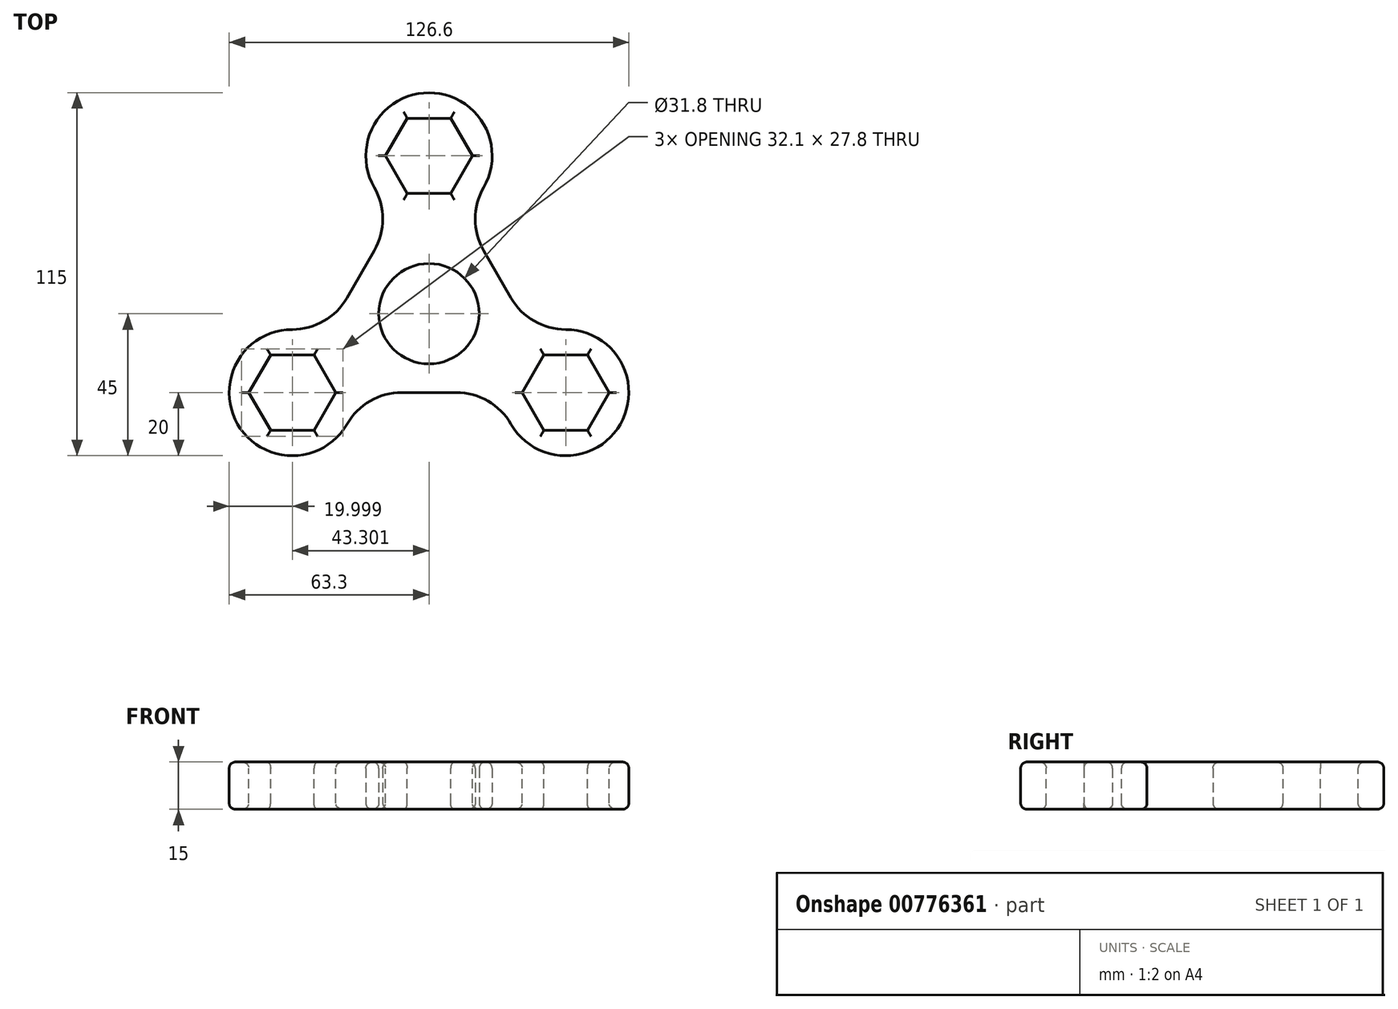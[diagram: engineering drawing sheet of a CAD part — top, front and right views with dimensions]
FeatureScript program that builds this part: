
annotation { "Feature Type Name" : "Feature", "Feature Type Description" : "" }
export const myFeature = defineFeature(function(context is Context, id is Id, definition is map)
    precondition{}
    {
        {
            var Q0;
            Q0=qCreatedBy(makeId("Top.planeOp"),FACE);
            var sketch = newSketch(context, id + "F0", { "sketchPlane" : qUnion([Q0])});
            skCircle(sketch, "E0", {"center": v(0, 0) * mm, "radius": 15.9 * mm});
            skLineSegment(sketch, "E1", {"start": v(0, 0) * mm, "end": v(0, 50) * mm, "construction": true});
            skLineSegment(sketch, "E2", {"start": v(0, 0) * mm, "end": v(-43.3, -25) * mm, "construction": true});
            skLineSegment(sketch, "E3", {"start": v(0, 0) * mm, "end": v(43.3, -25) * mm, "construction": true});
            skArc(sketch, "E4", {"start": v(17.32, 40) * mm, "mid": v(0, 70) * mm, "end": v(-17.32, 40) * mm});
            skArc(sketch, "E5", {"start": v(25.98, -35) * mm, "mid": v(60.62, -35) * mm, "end": v(43.3, -5) * mm});
            skArc(sketch, "E6", {"start": v(-43.3, -5) * mm, "mid": v(-60.62, -35) * mm, "end": v(-25.98, -35) * mm});
            skLineSegment(sketch, "E7", {"start": v(-17.32, 20) * mm, "end": v(-25.98, 5) * mm});
            skLineSegment(sketch, "E8", {"start": v(8.66, -25) * mm, "end": v(-8.66, -25) * mm});
            skLineSegment(sketch, "E9", {"start": v(17.32, 20) * mm, "end": v(25.98, 5) * mm});
            skPoint(sketch, "E10.visualSharp", {"position": v(-10, 32.68) * mm});
            skArc(sketch, "E10.filletArc", {"start": v(-17.32, 20) * mm, "mid": v(-14.64, 30) * mm, "end": v(-17.32, 40) * mm});
            skPoint(sketch, "E11.visualSharp", {"position": v(10, 32.68) * mm});
            skArc(sketch, "E11.filletArc", {"start": v(17.32, 40) * mm, "mid": v(14.64, 30) * mm, "end": v(17.32, 20) * mm});
            skPoint(sketch, "E12.visualSharp", {"position": v(33.3, -7.68) * mm});
            skArc(sketch, "E12.filletArc", {"start": v(25.98, 5) * mm, "mid": v(33.3, -2.32) * mm, "end": v(43.3, -5) * mm});
            skPoint(sketch, "E13.visualSharp", {"position": v(23.3, -25) * mm});
            skArc(sketch, "E13.filletArc", {"start": v(25.98, -35) * mm, "mid": v(18.66, -27.68) * mm, "end": v(8.66, -25) * mm});
            skPoint(sketch, "E14.visualSharp", {"position": v(-23.3, -25) * mm});
            skArc(sketch, "E14.filletArc", {"start": v(-8.66, -25) * mm, "mid": v(-18.66, -27.68) * mm, "end": v(-25.98, -35) * mm});
            skPoint(sketch, "E15.visualSharp", {"position": v(-33.3, -7.68) * mm});
            skArc(sketch, "E15.filletArc", {"start": v(-43.3, -5) * mm, "mid": v(-33.3, -2.32) * mm, "end": v(-25.98, 5) * mm});
            skSolve(sketch);
        }
        {
            var Q0;
            Q0=makeQuery(id+"F0.imprint","IMPRINT",FACE,{"disambiguationData":[TD([[makeQuery(id+"F0.imprint","IMPRINT",EDGE,{"derivedFrom":sQuery(id+"F0.wireOp",EDGE,"E0")}),-1.0]])]});
            extrude(context, id + "F1", {"entities" : qUnion([Q0]), "depth" : 15 * mm, "offsetDistance" : 25 * mm});
        }
        {
            var Q0;
            Q0=makeQuery(id+"F1.opExtrude","CAP_FACE",FACE,{"disambiguationData":[OSD([sQuery(id+"F0.wireOp",EDGE,"E0"),sQuery(id+"F0.wireOp",EDGE,"E4"),sQuery(id+"F0.wireOp",EDGE,"E5"),sQuery(id+"F0.wireOp",EDGE,"E6"),sQuery(id+"F0.wireOp",EDGE,"E7"),sQuery(id+"F0.wireOp",EDGE,"E8"),sQuery(id+"F0.wireOp",EDGE,"E9"),sQuery(id+"F0.wireOp",EDGE,"E10.filletArc"),sQuery(id+"F0.wireOp",EDGE,"E11.filletArc"),sQuery(id+"F0.wireOp",EDGE,"E12.filletArc"),sQuery(id+"F0.wireOp",EDGE,"E13.filletArc"),sQuery(id+"F0.wireOp",EDGE,"E14.filletArc"),sQuery(id+"F0.wireOp",EDGE,"E15.filletArc")])],"isStart":false});
            var sketch = newSketch(context, id + "F2", { "sketchPlane" : qUnion([Q0])});
            skLineSegment(sketch, "E16", {"start": v(0, 0) * mm, "end": v(0, 50) * mm, "construction": true});
            skLineSegment(sketch, "E17", {"start": v(0, 0) * mm, "end": v(43.3, -25) * mm, "construction": true});
            skLineSegment(sketch, "E18", {"start": v(0, 0) * mm, "end": v(-43.3, -25) * mm, "construction": true});
            skCircle(sketch, "E19.cCircle", {"center": v(-43.3, -25) * mm, "radius": 11.9 * mm, "construction": true});
            skLineSegment(sketch, "E19.0", {"start": v(-50.17, -13.1) * mm, "end": v(-36.43, -13.1) * mm});
            skLineSegment(sketch, "E19.1", {"start": v(-36.43, -13.1) * mm, "end": v(-29.56, -25) * mm});
            skLineSegment(sketch, "E19.2", {"start": v(-29.56, -25) * mm, "end": v(-36.43, -36.9) * mm});
            skLineSegment(sketch, "E19.3", {"start": v(-36.43, -36.9) * mm, "end": v(-50.17, -36.9) * mm});
            skLineSegment(sketch, "E19.4", {"start": v(-50.17, -36.9) * mm, "end": v(-57.04, -25) * mm});
            skLineSegment(sketch, "E19.5", {"start": v(-57.04, -25) * mm, "end": v(-50.17, -13.1) * mm});
            skPoint(sketch, "E19.0.midPoint", {"position": v(-43.3, -13.1) * mm});
            skCircle(sketch, "E20.cCircle", {"center": v(43.3, -25) * mm, "radius": 11.9 * mm, "construction": true});
            skLineSegment(sketch, "E20.0", {"start": v(36.43, -13.1) * mm, "end": v(50.17, -13.1) * mm});
            skLineSegment(sketch, "E20.1", {"start": v(50.17, -13.1) * mm, "end": v(57.04, -25) * mm});
            skLineSegment(sketch, "E20.2", {"start": v(57.04, -25) * mm, "end": v(50.17, -36.9) * mm});
            skLineSegment(sketch, "E20.3", {"start": v(50.17, -36.9) * mm, "end": v(36.43, -36.9) * mm});
            skLineSegment(sketch, "E20.4", {"start": v(36.43, -36.9) * mm, "end": v(29.56, -25) * mm});
            skLineSegment(sketch, "E20.5", {"start": v(29.56, -25) * mm, "end": v(36.43, -13.1) * mm});
            skPoint(sketch, "E20.0.midPoint", {"position": v(43.3, -13.1) * mm});
            skCircle(sketch, "E21.cCircle", {"center": v(0, 50) * mm, "radius": 11.9 * mm, "construction": true});
            skLineSegment(sketch, "E21.0", {"start": v(-6.87, 61.9) * mm, "end": v(6.87, 61.9) * mm});
            skLineSegment(sketch, "E21.1", {"start": v(6.87, 61.9) * mm, "end": v(13.74, 50) * mm});
            skLineSegment(sketch, "E21.2", {"start": v(13.74, 50) * mm, "end": v(6.87, 38.1) * mm});
            skLineSegment(sketch, "E21.3", {"start": v(6.87, 38.1) * mm, "end": v(-6.87, 38.1) * mm});
            skLineSegment(sketch, "E21.4", {"start": v(-6.87, 38.1) * mm, "end": v(-13.74, 50) * mm});
            skLineSegment(sketch, "E21.5", {"start": v(-13.74, 50) * mm, "end": v(-6.87, 61.9) * mm});
            skPoint(sketch, "E21.0.midPoint", {"position": v(0, 61.9) * mm});
            skSolve(sketch);
        }
        {
            var Q0;
            Q0=makeQuery(id+"F2.imprint","IMPRINT",FACE,{"disambiguationData":[TD([[makeQuery(id+"F2.imprint","IMPRINT",EDGE,{"derivedFrom":sQuery(id+"F2.wireOp",EDGE,"E21.0")}),-1.0]])]});
            var Q1;
            Q1=makeQuery(id+"F2.imprint","IMPRINT",FACE,{"disambiguationData":[TD([[makeQuery(id+"F2.imprint","IMPRINT",EDGE,{"derivedFrom":sQuery(id+"F2.wireOp",EDGE,"E19.0")}),-1.0]])]});
            var Q2;
            Q2=makeQuery(id+"F2.imprint","IMPRINT",FACE,{"disambiguationData":[TD([[makeQuery(id+"F2.imprint","IMPRINT",EDGE,{"derivedFrom":sQuery(id+"F2.wireOp",EDGE,"E20.0")}),-1.0]])]});
            extrude(context, id + "F3", {"entities" : qUnion([Q0, Q1, Q2]), "operationType" : NewBodyOperationType.REMOVE, "oppositeDirection" : true, "depth" : 25 * mm, "offsetDistance" : 25 * mm});
        }
        {
            var Q0;
            Q0=makeQuery(id+"F1.opExtrude","CAP_FACE",FACE,{"disambiguationData":[OSD([sQuery(id+"F0.wireOp",EDGE,"E0"),sQuery(id+"F0.wireOp",EDGE,"E4"),sQuery(id+"F0.wireOp",EDGE,"E5"),sQuery(id+"F0.wireOp",EDGE,"E6"),sQuery(id+"F0.wireOp",EDGE,"E7"),sQuery(id+"F0.wireOp",EDGE,"E8"),sQuery(id+"F0.wireOp",EDGE,"E9"),sQuery(id+"F0.wireOp",EDGE,"E10.filletArc"),sQuery(id+"F0.wireOp",EDGE,"E11.filletArc"),sQuery(id+"F0.wireOp",EDGE,"E12.filletArc"),sQuery(id+"F0.wireOp",EDGE,"E13.filletArc"),sQuery(id+"F0.wireOp",EDGE,"E14.filletArc"),sQuery(id+"F0.wireOp",EDGE,"E15.filletArc")])],"isStart":false});
            fillet(context, id + "F4", {"entities" : qUnion([Q0]), "radius" : 2 * mm, "tangentPropagation" : true, "allowEdgeOverflow" : false});
        }
        {
            var Q0;
            Q0=makeQuery(id+"F1.opExtrude","CAP_FACE",FACE,{"disambiguationData":[OSD([sQuery(id+"F0.wireOp",EDGE,"E0"),sQuery(id+"F0.wireOp",EDGE,"E4"),sQuery(id+"F0.wireOp",EDGE,"E5"),sQuery(id+"F0.wireOp",EDGE,"E6"),sQuery(id+"F0.wireOp",EDGE,"E7"),sQuery(id+"F0.wireOp",EDGE,"E8"),sQuery(id+"F0.wireOp",EDGE,"E9"),sQuery(id+"F0.wireOp",EDGE,"E10.filletArc"),sQuery(id+"F0.wireOp",EDGE,"E11.filletArc"),sQuery(id+"F0.wireOp",EDGE,"E12.filletArc"),sQuery(id+"F0.wireOp",EDGE,"E13.filletArc"),sQuery(id+"F0.wireOp",EDGE,"E14.filletArc"),sQuery(id+"F0.wireOp",EDGE,"E15.filletArc")])],"isStart":true});
            fillet(context, id + "F5", {"entities" : qUnion([Q0]), "radius" : 2 * mm, "tangentPropagation" : true, "allowEdgeOverflow" : false});
        }
    });
